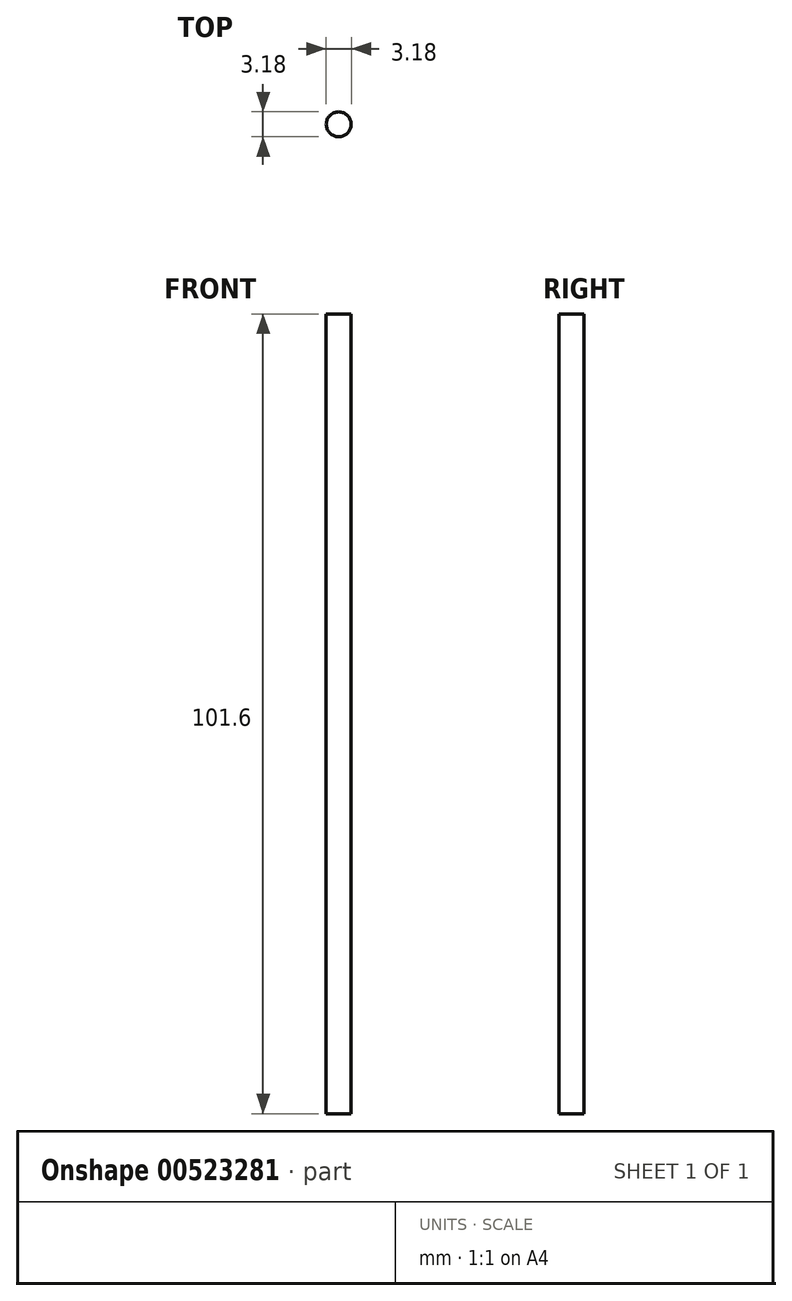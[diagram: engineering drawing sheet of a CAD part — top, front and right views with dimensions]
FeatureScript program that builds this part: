
annotation { "Feature Type Name" : "Feature", "Feature Type Description" : "" }
export const myFeature = defineFeature(function(context is Context, id is Id, definition is map)
    precondition{}
    {
        {
            var Q0;
            Q0=qCreatedBy(makeId("Top.planeOp"),FACE);
            var sketch = newSketch(context, id + "F0", { "sketchPlane" : qUnion([Q0])});
            skCircle(sketch, "E0", {"center": v(0, 0) * mm, "radius": 1.59 * mm});
            skSolve(sketch);
        }
        {
            var Q0;
            Q0=makeQuery(id+"F0.imprint","IMPRINT",FACE,{"disambiguationData":[TD([[makeQuery(id+"F0.imprint","IMPRINT",EDGE,{"derivedFrom":sQuery(id+"F0.wireOp",EDGE,"E0")}),1.0]])]});
            extrude(context, id + "F1", {"entities" : qUnion([Q0]), "depth" : 101.6 * mm, "offsetDistance" : 25.4 * mm});
        }
    });
